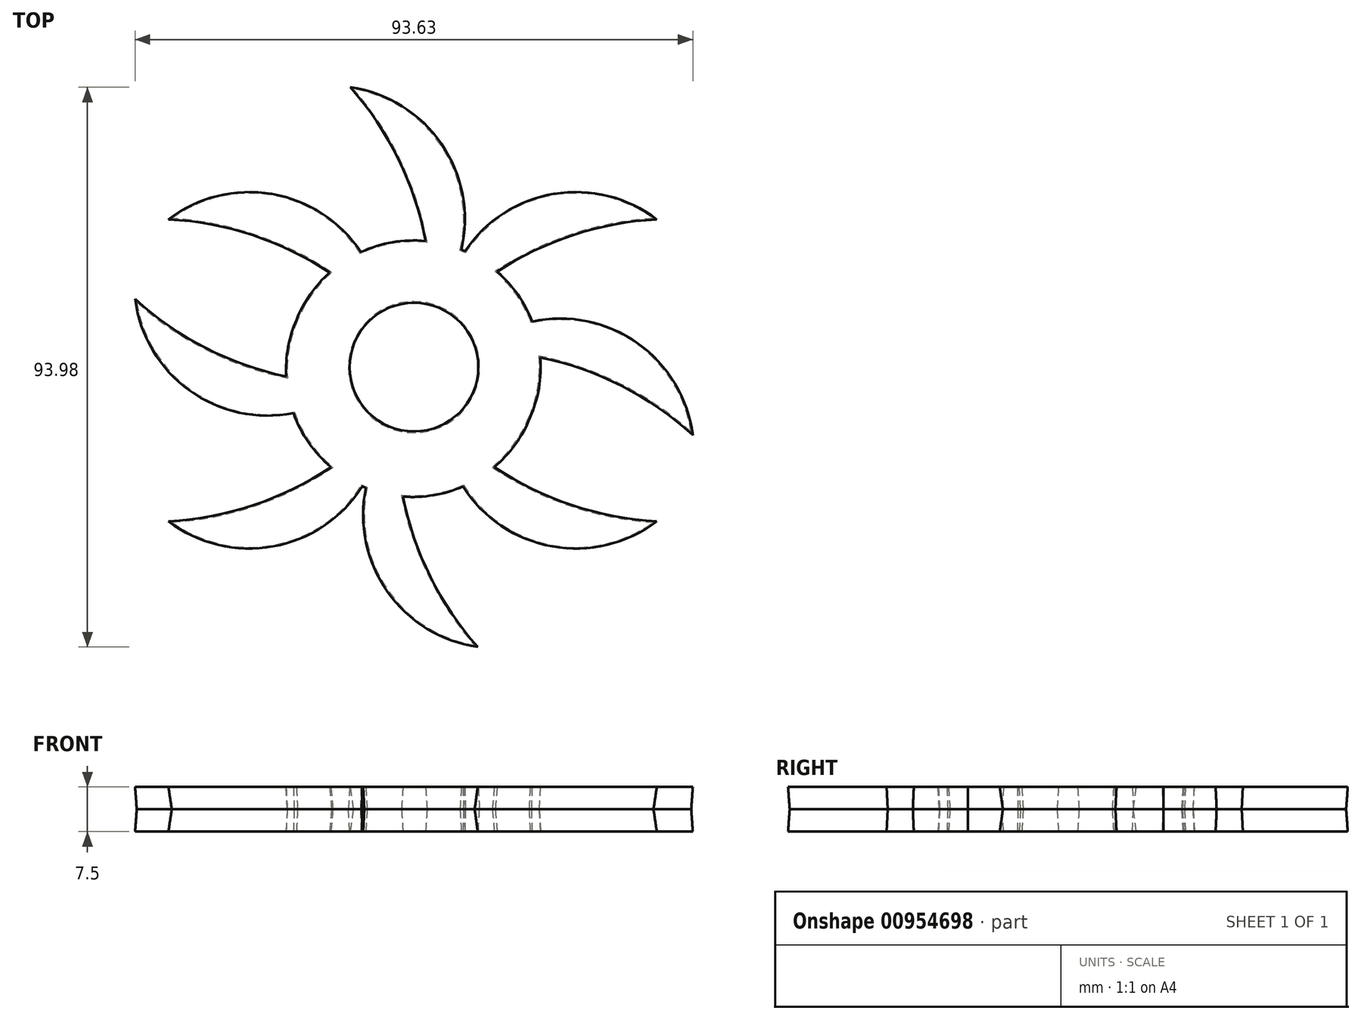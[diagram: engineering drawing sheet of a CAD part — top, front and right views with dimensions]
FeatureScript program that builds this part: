
annotation { "Feature Type Name" : "Feature", "Feature Type Description" : "" }
export const myFeature = defineFeature(function(context is Context, id is Id, definition is map)
    precondition{}
    {
        {
            var Q0;
            Q0=qCreatedBy(makeId("Top.planeOp"),FACE);
            var sketch = newSketch(context, id + "F0", { "sketchPlane" : qUnion([Q0])});
            skCircle(sketch, "E0", {"center": v(0, 0) * mm, "radius": 21.07 * mm});
            skArc(sketch, "E1", {"start": v(40.44, 25.5) * mm, "mid": v(23.13, 29.32) * mm, "end": v(8.54, 19.26) * mm});
            skArc(sketch, "E2", {"start": v(40.44, 25.5) * mm, "mid": v(26.3, 22.7) * mm, "end": v(13.39, 16.27) * mm});
            skArc(sketch, "E3.MirrorCS", {"start": v(40.44, -25.5) * mm, "mid": v(23.13, -29.32) * mm, "end": v(8.54, -19.26) * mm});
            skArc(sketch, "E4.MirrorCS", {"start": v(40.44, -25.5) * mm, "mid": v(26.3, -22.7) * mm, "end": v(13.39, -16.27) * mm});
            skArc(sketch, "E5.MirrorCS", {"start": v(-40.44, 25.5) * mm, "mid": v(-23.13, 29.32) * mm, "end": v(-8.54, 19.26) * mm});
            skArc(sketch, "E6.MirrorCS", {"start": v(-40.44, 25.5) * mm, "mid": v(-26.3, 22.7) * mm, "end": v(-13.39, 16.27) * mm});
            skArc(sketch, "E7.MirrorCS", {"start": v(-40.44, -25.5) * mm, "mid": v(-26.3, -22.7) * mm, "end": v(-13.39, -16.27) * mm});
            skArc(sketch, "E8.MirrorCS", {"start": v(-40.44, -25.5) * mm, "mid": v(-23.13, -29.32) * mm, "end": v(-8.54, -19.26) * mm});
            skLineSegment(sketch, "E9", {"start": v(-37.92, 16.2) * mm, "end": v(38.5, -15.8) * mm, "construction": true});
            skArc(sketch, "E10.MirrorCS", {"start": v(-46.32, 11.46) * mm, "mid": v(-34.4, 3.35) * mm, "end": v(-20.76, -1.34) * mm});
            skArc(sketch, "E11.MirrorCS", {"start": v(-46.32, 11.46) * mm, "mid": v(-36.9, -3.55) * mm, "end": v(-19.5, -6.9) * mm});
            skArc(sketch, "E12.MirrorCS", {"start": v(10.42, -46.18) * mm, "mid": v(2.5, -34.13) * mm, "end": v(-1.98, -20.42) * mm});
            skArc(sketch, "E13.MirrorCS", {"start": v(10.42, -46.18) * mm, "mid": v(-4.44, -36.52) * mm, "end": v(-7.51, -19.06) * mm});
            skArc(sketch, "E14.MirrorCS", {"start": v(46.77, -10.39) * mm, "mid": v(34.85, -2.28) * mm, "end": v(21.21, 2.41) * mm});
            skArc(sketch, "E15.MirrorCS", {"start": v(46.77, -10.39) * mm, "mid": v(37.35, 4.62) * mm, "end": v(19.94, 7.97) * mm});
            skArc(sketch, "E16.MirrorCS", {"start": v(-9.97, 47.25) * mm, "mid": v(-2.05, 35.2) * mm, "end": v(2.43, 21.5) * mm});
            skArc(sketch, "E17.MirrorCS", {"start": v(-9.97, 47.25) * mm, "mid": v(4.89, 37.6) * mm, "end": v(7.96, 20.14) * mm});
            skCircle(sketch, "E18.MirrorC", {"center": v(0.23, 0.54) * mm, "radius": 21.07 * mm});
            skLineSegment(sketch, "E19", {"start": v(45.1, 21.82) * mm, "end": v(-48, -19.88) * mm, "construction": true});
            skCircle(sketch, "E20", {"center": v(0.23, 0.54) * mm, "radius": 11 * mm});
            skSolve(sketch);
        }
        {
            var Q0;
            Q0 = qSketchRegion(id + "F0", true);
            extrude(context, id + "F1", {"entities" : qUnion([Q0]), "endBound" : BoundingType.SYMMETRIC, "depth" : 7.5 * mm, "offsetDistance" : 25 * mm, "hasDraft" : true, "draftAngle" : 3 * degree});
        }
        {
            var Q0;
            Q0 = qSketchRegion(id + "F0", true);
            extrude(context, id + "F2", {"entities" : qUnion([Q0]), "operationType" : NewBodyOperationType.ADD, "endBound" : BoundingType.SYMMETRIC, "depth" : 7 * mm, "offsetDistance" : 25 * mm});
        }
    });
